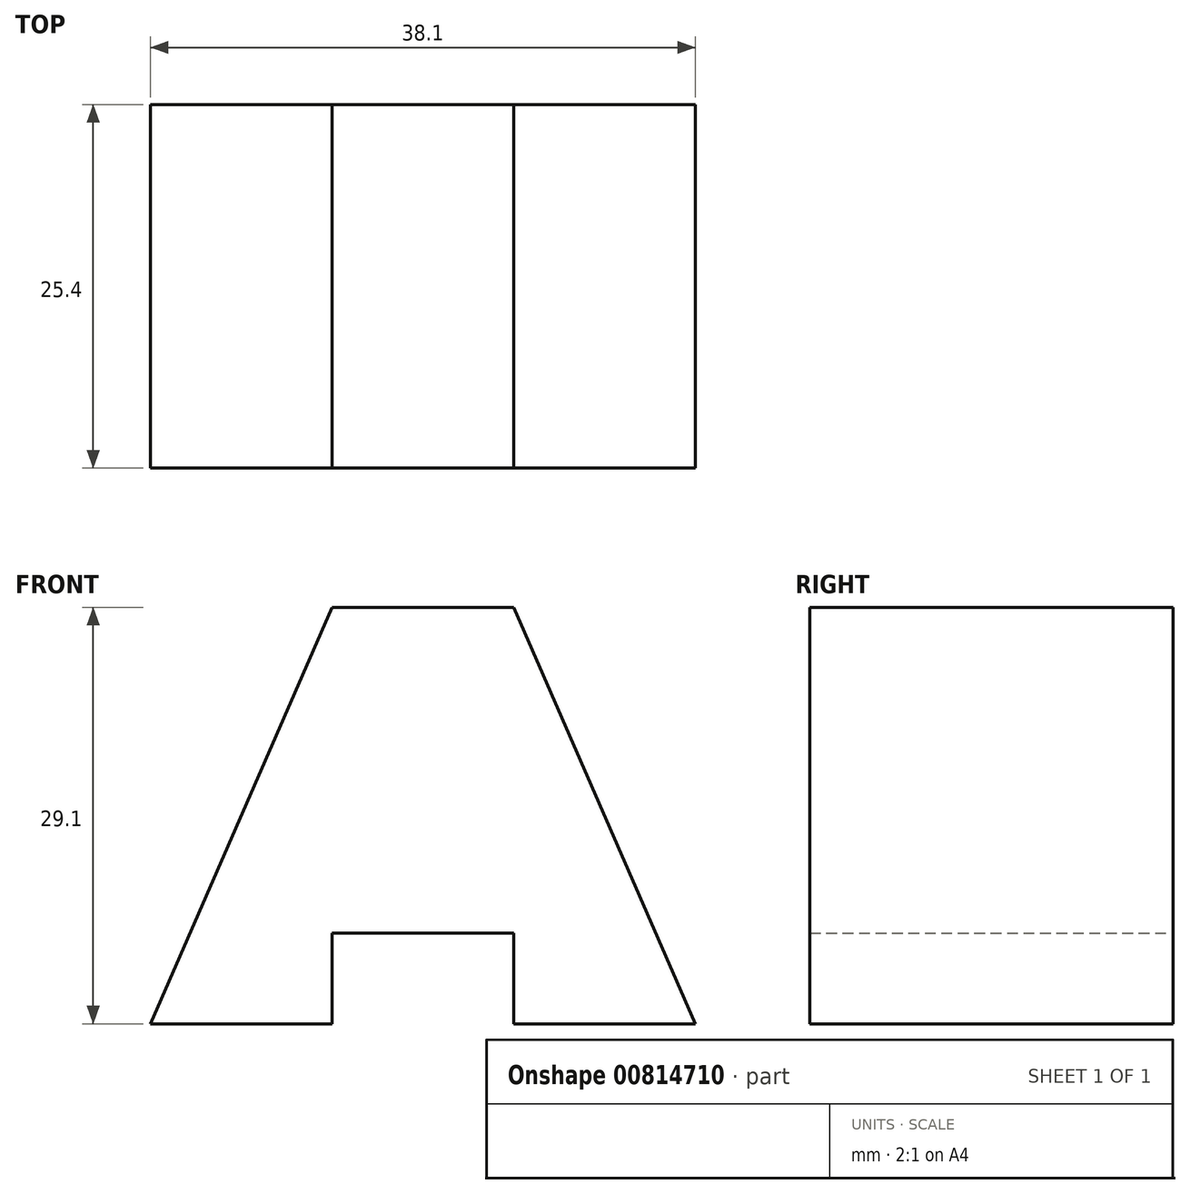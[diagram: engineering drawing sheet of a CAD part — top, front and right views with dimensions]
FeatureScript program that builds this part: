
annotation { "Feature Type Name" : "Feature", "Feature Type Description" : "" }
export const myFeature = defineFeature(function(context is Context, id is Id, definition is map)
    precondition{}
    {
        {
            var Q0;
            Q0=qCreatedBy(makeId("Front.planeOp"),FACE);
            var sketch = newSketch(context, id + "F0", { "sketchPlane" : qUnion([Q0])});
            skLineSegment(sketch, "E0", {"start": v(0, 0) * mm, "end": v(12.7, 0) * mm});
            skLineSegment(sketch, "E1", {"start": v(12.7, 0) * mm, "end": v(12.7, 6.35) * mm});
            skLineSegment(sketch, "E2", {"start": v(12.7, 6.35) * mm, "end": v(25.4, 6.35) * mm});
            skLineSegment(sketch, "E3", {"start": v(25.4, 6.35) * mm, "end": v(25.4, 0) * mm});
            skLineSegment(sketch, "E4", {"start": v(25.4, 0) * mm, "end": v(38.1, 0) * mm});
            skLineSegment(sketch, "E5", {"start": v(38.1, 0) * mm, "end": v(25.4, 29.1) * mm});
            skLineSegment(sketch, "E6", {"start": v(25.4, 29.1) * mm, "end": v(12.7, 29.1) * mm});
            skLineSegment(sketch, "E7", {"start": v(12.7, 29.1) * mm, "end": v(0, 0) * mm});
            skSolve(sketch);
        }
        {
            var Q0;
            Q0=makeQuery(id+"F0.imprint","IMPRINT",FACE,{"disambiguationData":[TD([[makeQuery(id+"F0.imprint","IMPRINT",EDGE,{"derivedFrom":sQuery(id+"F0.wireOp",EDGE,"E0")}),1.0]])]});
            extrude(context, id + "F1", {"entities" : qUnion([Q0]), "depth" : 25.4 * mm, "offsetDistance" : 25.4 * mm});
        }
    });
